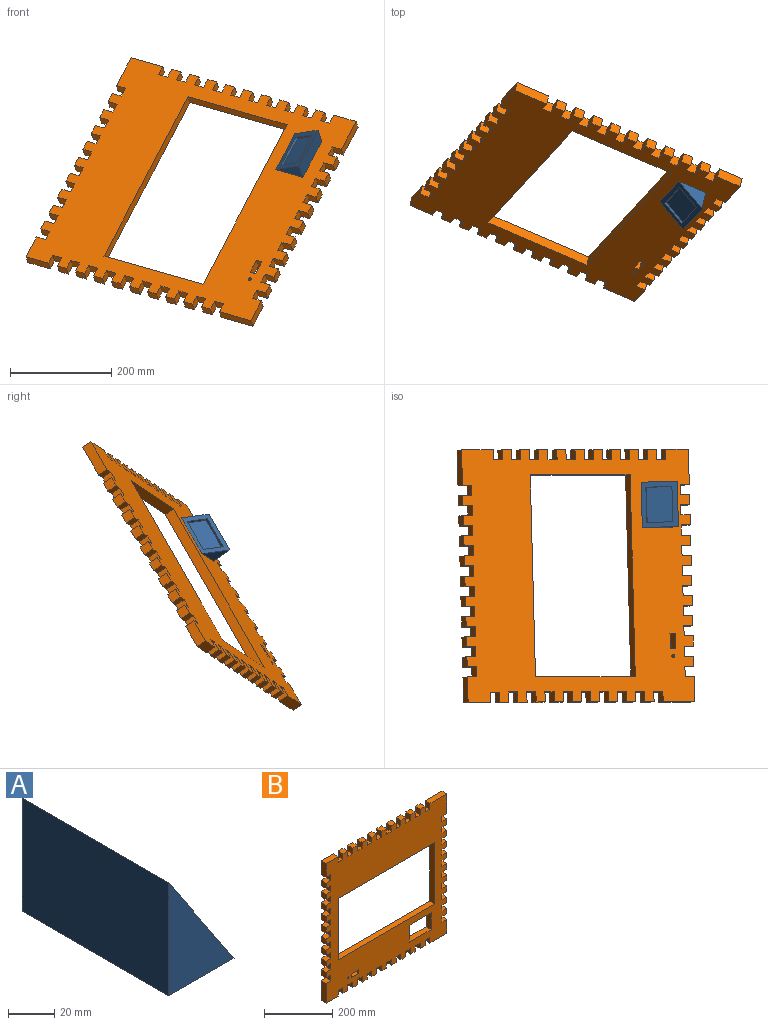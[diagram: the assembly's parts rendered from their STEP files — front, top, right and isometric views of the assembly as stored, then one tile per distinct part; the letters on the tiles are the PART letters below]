
ASSEMBLY  parts=2 mates=1
PART A: 10 faces, bbox 40x90x60 mm
  f0: plane 90x60mm, normal (0.83,0,0.55), area 2850mm2, adj f1,f2,f3,f4,f5,f6,f7,f8
  f1: plane 90x60mm, normal (-1,0,0), area 5400mm2, adj f0,f2,f3,f4
  f2: plane 90x40mm, normal (0,0,-1), area 3600mm2, adj f0,f1,f3,f4
  f3: plane 60x40mm, normal (0,-1,0), area 1200mm2, adj f0,f1,f2
  f4: plane 60x40mm, normal (0,1,0), area 1200mm2, adj f0,f1,f2
  f5: plane 70x4.16mm, normal (0.55,0,-0.83), area 350mm2, adj f0,f6,f8,f9
  f6: plane 46.04x33mm, normal (0,1,0), area 260mm2, adj f0,f5,f7,f9
  f7: plane 70x4.16mm, normal (-0.55,0,0.83), area 350mm2, adj f0,f6,f8,f9
  f8: plane 46.04x33mm, normal (0,-1,0), area 260mm2, adj f0,f5,f7,f9
  f9: plane 70x43.27mm, normal (0.83,0,0.55), area 3640mm2, adj f5,f6,f7,f8
PART B: 183 faces, bbox 500x20x500 mm
  f0: plane 500x500mm, normal (0,1,0), area 139809.6mm2, adj f2,f3,f4,f5,f6,f7,f8,f9
  f1: plane 500x500mm, normal (0,-1,0), area 140211.7mm2, adj f2,f3,f4,f5,f6,f7,f8,f9
  f2: plane 20x20mm, normal (1,0,0), area 400mm2, adj f0,f1,f169,f171
  f3: plane 20x20mm, normal (1,0,0), area 400mm2, adj f0,f1,f166,f168
  f4: plane 20x20mm, normal (1,0,0), area 400mm2, adj f0,f1,f163,f165
  f5: plane 20x20mm, normal (1,0,0), area 400mm2, adj f0,f1,f160,f162
  f6: plane 20x20mm, normal (1,0,0), area 400mm2, adj f0,f1,f157,f159
  f7: plane 20x20mm, normal (1,0,0), area 400mm2, adj f0,f1,f154,f156
  f8: plane 20x20mm, normal (1,0,0), area 400mm2, adj f0,f1,f151,f153
  f9: plane 20x20mm, normal (1,0,0), area 400mm2, adj f0,f1,f148,f150
  f10: plane 20x20mm, normal (1,0,0), area 400mm2, adj f0,f1,f145,f147
  f11: plane 50x20mm, normal (1,0,0), area 1000mm2, adj f0,f1,f22,f144
  f12: plane 70x20mm, normal (-1,0,0), area 1400mm2, adj f0,f1,f43,f133
  f13: plane 20x20mm, normal (-1,0,0), area 400mm2, adj f0,f1,f130,f135
  f14: plane 20x20mm, normal (-1,0,0), area 400mm2, adj f0,f1,f127,f132
  f15: plane 20x20mm, normal (-1,0,0), area 400mm2, adj f0,f1,f124,f129
  f16: plane 20x20mm, normal (-1,0,0), area 400mm2, adj f0,f1,f121,f126
  f17: plane 20x20mm, normal (-1,0,0), area 400mm2, adj f0,f1,f118,f123
  f18: plane 20x20mm, normal (-1,0,0), area 400mm2, adj f0,f1,f115,f120
  f19: plane 20x20mm, normal (-1,0,0), area 400mm2, adj f0,f1,f112,f117
  f20: plane 20x20mm, normal (-1,0,0), area 400mm2, adj f0,f1,f109,f114
  f21: plane 20x20mm, normal (-1,0,0), area 400mm2, adj f0,f1,f106,f111
  f22: plane 70x20mm, normal (0,0,-1), area 1400mm2, adj f0,f1,f11,f101
  f23: plane 70x20mm, normal (0,0,1), area 1400mm2, adj f0,f1,f44,f103
  f24: plane 20x20mm, normal (0,0,-1), area 400mm2, adj f0,f1,f95,f100
  f25: plane 20x20mm, normal (0,0,1), area 400mm2, adj f0,f1,f97,f104
  f26: plane 20x20mm, normal (0,0,-1), area 400mm2, adj f0,f1,f89,f94
  f27: plane 20x20mm, normal (0,0,1), area 400mm2, adj f0,f1,f91,f98
  f28: plane 20x20mm, normal (0,0,-1), area 400mm2, adj f0,f1,f83,f88
  f29: plane 20x20mm, normal (0,0,1), area 400mm2, adj f0,f1,f85,f92
  f30: plane 20x20mm, normal (0,0,-1), area 400mm2, adj f0,f1,f77,f82
  f31: plane 20x20mm, normal (0,0,1), area 400mm2, adj f0,f1,f79,f86
  f32: plane 20x20mm, normal (0,0,-1), area 400mm2, adj f0,f1,f71,f76
  f33: plane 20x20mm, normal (0,0,1), area 400mm2, adj f0,f1,f73,f80
  f34: plane 20x20mm, normal (0,0,-1), area 400mm2, adj f0,f1,f65,f70
  f35: plane 20x20mm, normal (0,0,1), area 400mm2, adj f0,f1,f67,f74
  f36: plane 20x20mm, normal (0,0,-1), area 400mm2, adj f0,f1,f59,f64
  f37: plane 20x20mm, normal (0,0,1), area 400mm2, adj f0,f1,f61,f68
  f38: plane 20x20mm, normal (0,0,-1), area 400mm2, adj f0,f1,f53,f58
  f39: plane 20x20mm, normal (0,0,1), area 400mm2, adj f0,f1,f55,f62
  f40: plane 20x20mm, normal (0,0,-1), area 400mm2, adj f0,f1,f47,f52
  f41: plane 20x20mm, normal (0,0,1), area 400mm2, adj f0,f1,f49,f56
  f42: plane 50x20mm, normal (-1,0,0), area 1000mm2, adj f0,f1,f45,f108
  f43: plane 50x20mm, normal (0,0,-1), area 1000mm2, adj f0,f1,f12,f46
  f44: plane 70x20mm, normal (1,0,0), area 1400mm2, adj f0,f1,f23,f172
  f45: plane 50x20mm, normal (0,0,1), area 1000mm2, adj f0,f1,f42,f50
  f46: plane 20x20mm, normal (1,0,0), area 400mm2, adj f0,f1,f43,f48
  f47: plane 20x20mm, normal (-1,0,0), area 400mm2, adj f0,f1,f40,f48
  f48: plane 20x20mm, normal (0,0,-1), area 400mm2, adj f0,f1,f46,f47
  f49: plane 20x20mm, normal (-1,0,0), area 400mm2, adj f0,f1,f41,f51
  f50: plane 20x20mm, normal (1,0,0), area 400mm2, adj f0,f1,f45,f51
  f51: plane 20x20mm, normal (0,0,1), area 400mm2, adj f0,f1,f49,f50
  f52: plane 20x20mm, normal (1,0,0), area 400mm2, adj f0,f1,f40,f54
  f53: plane 20x20mm, normal (-1,0,0), area 400mm2, adj f0,f1,f38,f54
  f54: plane 20x20mm, normal (0,0,-1), area 400mm2, adj f0,f1,f52,f53
  f55: plane 20x20mm, normal (-1,0,0), area 400mm2, adj f0,f1,f39,f57
  f56: plane 20x20mm, normal (1,0,0), area 400mm2, adj f0,f1,f41,f57
  f57: plane 20x20mm, normal (0,0,1), area 400mm2, adj f0,f1,f55,f56
  f58: plane 20x20mm, normal (1,0,0), area 400mm2, adj f0,f1,f38,f60
  f59: plane 20x20mm, normal (-1,0,0), area 400mm2, adj f0,f1,f36,f60
  f60: plane 20x20mm, normal (0,0,-1), area 400mm2, adj f0,f1,f58,f59
  f61: plane 20x20mm, normal (-1,0,0), area 400mm2, adj f0,f1,f37,f63
  f62: plane 20x20mm, normal (1,0,0), area 400mm2, adj f0,f1,f39,f63
  f63: plane 20x20mm, normal (0,0,1), area 400mm2, adj f0,f1,f61,f62
  f64: plane 20x20mm, normal (1,0,0), area 400mm2, adj f0,f1,f36,f66
  f65: plane 20x20mm, normal (-1,0,0), area 400mm2, adj f0,f1,f34,f66
  f66: plane 20x20mm, normal (0,0,-1), area 400mm2, adj f0,f1,f64,f65
  f67: plane 20x20mm, normal (-1,0,0), area 400mm2, adj f0,f1,f35,f69
  f68: plane 20x20mm, normal (1,0,0), area 400mm2, adj f0,f1,f37,f69
  f69: plane 20x20mm, normal (0,0,1), area 400mm2, adj f0,f1,f67,f68
  f70: plane 20x20mm, normal (1,0,0), area 400mm2, adj f0,f1,f34,f72
  f71: plane 20x20mm, normal (-1,0,0), area 400mm2, adj f0,f1,f32,f72
  f72: plane 20x20mm, normal (0,0,-1), area 400mm2, adj f0,f1,f70,f71
  f73: plane 20x20mm, normal (-1,0,0), area 400mm2, adj f0,f1,f33,f75
  f74: plane 20x20mm, normal (1,0,0), area 400mm2, adj f0,f1,f35,f75
  f75: plane 20x20mm, normal (0,0,1), area 400mm2, adj f0,f1,f73,f74
  f76: plane 20x20mm, normal (1,0,0), area 400mm2, adj f0,f1,f32,f78
  f77: plane 20x20mm, normal (-1,0,0), area 400mm2, adj f0,f1,f30,f78
  f78: plane 20x20mm, normal (0,0,-1), area 400mm2, adj f0,f1,f76,f77
  f79: plane 20x20mm, normal (-1,0,0), area 400mm2, adj f0,f1,f31,f81
  f80: plane 20x20mm, normal (1,0,0), area 400mm2, adj f0,f1,f33,f81
  f81: plane 20x20mm, normal (0,0,1), area 400mm2, adj f0,f1,f79,f80
  f82: plane 20x20mm, normal (1,0,0), area 400mm2, adj f0,f1,f30,f84
  f83: plane 20x20mm, normal (-1,0,0), area 400mm2, adj f0,f1,f28,f84
  f84: plane 20x20mm, normal (0,0,-1), area 400mm2, adj f0,f1,f82,f83
  f85: plane 20x20mm, normal (-1,0,0), area 400mm2, adj f0,f1,f29,f87
  f86: plane 20x20mm, normal (1,0,0), area 400mm2, adj f0,f1,f31,f87
  f87: plane 20x20mm, normal (0,0,1), area 400mm2, adj f0,f1,f85,f86
  f88: plane 20x20mm, normal (1,0,0), area 400mm2, adj f0,f1,f28,f90
  f89: plane 20x20mm, normal (-1,0,0), area 400mm2, adj f0,f1,f26,f90
  f90: plane 20x20mm, normal (0,0,-1), area 400mm2, adj f0,f1,f88,f89
  f91: plane 20x20mm, normal (-1,0,0), area 400mm2, adj f0,f1,f27,f93
  f92: plane 20x20mm, normal (1,0,0), area 400mm2, adj f0,f1,f29,f93
  f93: plane 20x20mm, normal (0,0,1), area 400mm2, adj f0,f1,f91,f92
  f94: plane 20x20mm, normal (1,0,0), area 400mm2, adj f0,f1,f26,f96
  f95: plane 20x20mm, normal (-1,0,0), area 400mm2, adj f0,f1,f24,f96
  f96: plane 20x20mm, normal (0,0,-1), area 400mm2, adj f0,f1,f94,f95
  f97: plane 20x20mm, normal (-1,0,0), area 400mm2, adj f0,f1,f25,f99
  f98: plane 20x20mm, normal (1,0,0), area 400mm2, adj f0,f1,f27,f99
  f99: plane 20x20mm, normal (0,0,1), area 400mm2, adj f0,f1,f97,f98
  f100: plane 20x20mm, normal (1,0,0), area 400mm2, adj f0,f1,f24,f102
  f101: plane 20x20mm, normal (-1,0,0), area 400mm2, adj f0,f1,f22,f102
  f102: plane 20x20mm, normal (0,0,-1), area 400mm2, adj f0,f1,f100,f101
  f103: plane 20x20mm, normal (-1,0,0), area 400mm2, adj f0,f1,f23,f105
  f104: plane 20x20mm, normal (1,0,0), area 400mm2, adj f0,f1,f25,f105
  f105: plane 20x20mm, normal (0,0,1), area 400mm2, adj f0,f1,f103,f104
  f106: plane 20x20mm, normal (0,0,1), area 400mm2, adj f0,f1,f21,f107
  f107: plane 20x20mm, normal (-1,0,0), area 400mm2, adj f0,f1,f106,f108
  f108: plane 20x20mm, normal (0,0,-1), area 400mm2, adj f0,f1,f42,f107
  f109: plane 20x20mm, normal (0,0,1), area 400mm2, adj f0,f1,f20,f110
  f110: plane 20x20mm, normal (-1,0,0), area 400mm2, adj f0,f1,f109,f111
  f111: plane 20x20mm, normal (0,0,-1), area 400mm2, adj f0,f1,f21,f110
  f112: plane 20x20mm, normal (0,0,1), area 400mm2, adj f0,f1,f19,f113
  f113: plane 20x20mm, normal (-1,0,0), area 400mm2, adj f0,f1,f112,f114
  f114: plane 20x20mm, normal (0,0,-1), area 400mm2, adj f0,f1,f20,f113
  f115: plane 20x20mm, normal (0,0,1), area 400mm2, adj f0,f1,f18,f116
  f116: plane 20x20mm, normal (-1,0,0), area 400mm2, adj f0,f1,f115,f117
  f117: plane 20x20mm, normal (0,0,-1), area 400mm2, adj f0,f1,f19,f116
  f118: plane 20x20mm, normal (0,0,1), area 400mm2, adj f0,f1,f17,f119
  f119: plane 20x20mm, normal (-1,0,0), area 400mm2, adj f0,f1,f118,f120
  f120: plane 20x20mm, normal (0,0,-1), area 400mm2, adj f0,f1,f18,f119
  f121: plane 20x20mm, normal (0,0,1), area 400mm2, adj f0,f1,f16,f122
  f122: plane 20x20mm, normal (-1,0,0), area 400mm2, adj f0,f1,f121,f123
  f123: plane 20x20mm, normal (0,0,-1), area 400mm2, adj f0,f1,f17,f122
  f124: plane 20x20mm, normal (0,0,1), area 400mm2, adj f0,f1,f15,f125
  f125: plane 20x20mm, normal (-1,0,0), area 400mm2, adj f0,f1,f124,f126
  f126: plane 20x20mm, normal (0,0,-1), area 400mm2, adj f0,f1,f16,f125
  f127: plane 20x20mm, normal (0,0,1), area 400mm2, adj f0,f1,f14,f128
  f128: plane 20x20mm, normal (-1,0,0), area 400mm2, adj f0,f1,f127,f129
  f129: plane 20x20mm, normal (0,0,-1), area 400mm2, adj f0,f1,f15,f128
  f130: plane 20x20mm, normal (0,0,1), area 400mm2, adj f0,f1,f13,f131
  f131: plane 20x20mm, normal (-1,0,0), area 400mm2, adj f0,f1,f130,f132
  f132: plane 20x20mm, normal (0,0,-1), area 400mm2, adj f0,f1,f14,f131
  f133: plane 20x20mm, normal (0,0,1), area 400mm2, adj f0,f1,f12,f134
  f134: plane 20x20mm, normal (-1,0,0), area 400mm2, adj f0,f1,f133,f135
  f135: plane 20x20mm, normal (0,0,-1), area 400mm2, adj f0,f1,f13,f134
  f136: plane 220x20mm, normal (1,0,0), area 4400mm2, adj f0,f1,f137,f139
  f137: plane 400x20mm, normal (0,0,1), area 8000mm2, adj f0,f1,f136,f138
  f138: plane 220x20mm, normal (-1,0,0), area 4400mm2, adj f0,f1,f137,f139
  f139: plane 400x20mm, normal (0,0,-1), area 8000mm2, adj f0,f1,f136,f138
  f140: cylinder r=8mm len=16mm, axis (0,1,0), area 251.3mm2, adj f0,f141
  f141: plane 16x16mm, normal (0,1,0), area 201.1mm2, adj f140
  f142: cylinder r=8mm len=16mm, axis (0,1,0), area 251.3mm2, adj f0,f143
  f143: plane 16x16mm, normal (0,1,0), area 201.1mm2, adj f142
  f144: plane 20x20mm, normal (0,0,1), area 400mm2, adj f0,f1,f11,f146
  f145: plane 20x20mm, normal (0,0,-1), area 400mm2, adj f0,f1,f10,f146
  f146: plane 20x20mm, normal (1,0,0), area 400mm2, adj f0,f1,f144,f145
  f147: plane 20x20mm, normal (0,0,1), area 400mm2, adj f0,f1,f10,f149
  f148: plane 20x20mm, normal (0,0,-1), area 400mm2, adj f0,f1,f9,f149
  f149: plane 20x20mm, normal (1,0,0), area 400mm2, adj f0,f1,f147,f148
  f150: plane 20x20mm, normal (0,0,1), area 400mm2, adj f0,f1,f9,f152
  f151: plane 20x20mm, normal (0,0,-1), area 400mm2, adj f0,f1,f8,f152
  f152: plane 20x20mm, normal (1,0,0), area 400mm2, adj f0,f1,f150,f151
  f153: plane 20x20mm, normal (0,0,1), area 400mm2, adj f0,f1,f8,f155
  f154: plane 20x20mm, normal (0,0,-1), area 400mm2, adj f0,f1,f7,f155
  f155: plane 20x20mm, normal (1,0,0), area 400mm2, adj f0,f1,f153,f154
  f156: plane 20x20mm, normal (0,0,1), area 400mm2, adj f0,f1,f7,f158
  f157: plane 20x20mm, normal (0,0,-1), area 400mm2, adj f0,f1,f6,f158
  f158: plane 20x20mm, normal (1,0,0), area 400mm2, adj f0,f1,f156,f157
  f159: plane 20x20mm, normal (0,0,1), area 400mm2, adj f0,f1,f6,f161
  f160: plane 20x20mm, normal (0,0,-1), area 400mm2, adj f0,f1,f5,f161
  f161: plane 20x20mm, normal (1,0,0), area 400mm2, adj f0,f1,f159,f160
  f162: plane 20x20mm, normal (0,0,1), area 400mm2, adj f0,f1,f5,f164
  f163: plane 20x20mm, normal (0,0,-1), area 400mm2, adj f0,f1,f4,f164
  f164: plane 20x20mm, normal (1,0,0), area 400mm2, adj f0,f1,f162,f163
  f165: plane 20x20mm, normal (0,0,1), area 400mm2, adj f0,f1,f4,f167
  f166: plane 20x20mm, normal (0,0,-1), area 400mm2, adj f0,f1,f3,f167
  f167: plane 20x20mm, normal (1,0,0), area 400mm2, adj f0,f1,f165,f166
  f168: plane 20x20mm, normal (0,0,1), area 400mm2, adj f0,f1,f3,f170
  f169: plane 20x20mm, normal (0,0,-1), area 400mm2, adj f0,f1,f2,f170
  f170: plane 20x20mm, normal (1,0,0), area 400mm2, adj f0,f1,f168,f169
  f171: plane 20x20mm, normal (0,0,1), area 400mm2, adj f0,f1,f2,f173
  f172: plane 20x20mm, normal (0,0,-1), area 400mm2, adj f0,f1,f44,f173
  f173: plane 20x20mm, normal (1,0,0), area 400mm2, adj f0,f1,f171,f172
  f174: plane 60x20mm, normal (-1,0,0), area 1200mm2, adj f0,f1,f175,f177
  f175: plane 90x20mm, normal (0,0,-1), area 1800mm2, adj f0,f1,f174,f176
  f176: plane 60x20mm, normal (1,0,0), area 1200mm2, adj f0,f1,f175,f177
  f177: plane 90x20mm, normal (0,0,1), area 1800mm2, adj f0,f1,f174,f176
  f178: cylinder r=3mm len=20mm, axis (0,1,0), area 377mm2, adj f0,f1
  f179: plane 30x20mm, normal (0,0,-1), area 600mm2, adj f0,f1,f180,f182
  f180: plane 20x12mm, normal (-1,0,0), area 240mm2, adj f0,f1,f179,f181
  f181: plane 30x20mm, normal (0,0,1), area 600mm2, adj f0,f1,f180,f182
  f182: plane 20x12mm, normal (1,0,0), area 240mm2, adj f0,f1,f179,f181
PLACE A rot(axis=(0.21,-0.75,-0.63),103.9deg) t=(1039.48,585.33,245.9)mm
PLACE B rot(axis=(-0.48,-0.86,0.14),76.2deg) t=(804.88,586.34,134.56)mm
MATE fastened A.f2 <-> B.f177  axis (0.89,-0.38,-0.25) through (1037.4,540.13,215.89)mm
